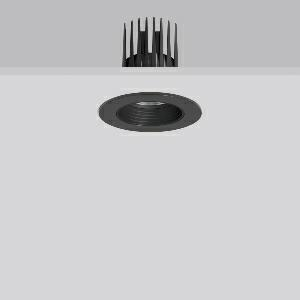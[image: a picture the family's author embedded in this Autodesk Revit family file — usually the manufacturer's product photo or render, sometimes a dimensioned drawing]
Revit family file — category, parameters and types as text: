
# Revit family: heledon_mini_e_901746_003_2_690c
name_source: partatom
category: Lighting Fixtures
units: mm (PartAtom-declared; Revit-internal decimal feet)

## family parameters
Cut with Voids When Loaded = No
Host = Face
Light Source = No
Part Type = Normal
Room Calculation Point = No
Round Connector Dimension = Use Diameter
Shared = No

## types (1)
- HELEDON mini E (1 x LED Modul 927, 2150 lm, 2700)
    Apparent Load = 20 VA
    Approval mark = CE
    CIE Flux Codes = 80 99 100 100 100
    Color Rendering = 92
    Color Temperature = 2700
    Default Elevation = 1800 mm
    Description = Series: HELEDON mini
Round recessed downlight. Housing: die-cast aluminium, powder-coated. Black plastic ring and recessed LED to prevent glare from the side. Optical assembly with lens made of plastic (polycarbonate) for the best homogeneous light distribution - can be changed without tools. Best colour rendering index Ra>90. Suitable for Recessed ceiling mounting. Installation without tools thanks to spring fastening system. Including separate LED converter with connecting cable 600 mm.High quality converter without flickering and stroboscopic effect. Through-wiring box (5 pole) available as accessory. The following accessories can be mounted without use of tools: interchangeable lenses, decorative glasses, honeycomb louvre, clear and frosted diffusers, white interchangeable plastic ring. 
Colour: deep black, matt (RAL 9005)
Diameter: 124 mm
Height: 3 mm
Cut-out diameter: 114 mm
Recess height: 170 mm
Luminaire: recess height: 120 mm
Lamp: LED
Socket: without socket
Colour temperature: 2700K
Colour rendering index (CRI): 92
System power: 20 W
Rated luminous flux: 2150 lm
Luminous efficiency: 108 lm/W
Control gear: Regulated power supply
Protection class: II
Type of protection: IP 20
    Height = 0 mm  [stored 0 ft]
    Lamp = 1 x LED Modul 927
    Lamp Light Flux = 2150 lm
    Lamp count = 1
    Length = 124 mm  [stored 0.406824 ft]
    Lifetime = 50000 h
    Luminous efficacy = 108 lm/W
    Manufacturer = RZB
    ModVariant = No
    Model = 901746.003.2
    Mounting Place = Ceiling
    Mounting Type = Recessed
    Number of Poles = 1
    OnlyDefault = Yes
    Power Factor = 1
    Product Name = HELEDON mini E
    Product group = Recessed downlights
    ProductGroupID = 402
    Protection Class = Protection class II
    Protection Degree = IP 20
    RLX_Detail_Level = 1
    RLX_Emergency_Light_Flux = 0 lm
    RLX_Emergency_Type = 0
    RLX_Emergency_Type_DB = No
    RlxData = <blob elided: 127465 chars, md5=cc047ce0>
    Socket = socket
    Standby Power = 0 W
    System Light Flux = 2150 lm
    System Power = 20 W
    Type Comments = Product without accessories
    Type Image = 901656.003.jpg
    URL = http://relux.com
    VarID = ---
    Voltage = 230 V
    Voltage Range = 220-240 V
    Weight = 0.00 kg
    Width = 0 mm  [stored 0 ft]

note: [stored X ft] marks values corroborated as IEEE doubles in the binary element streams (Revit-internal decimal feet)

## geometry (parser evidence)
native form markers: Blend x4, Sweep x11
no freeform markers — native parametric forms only
